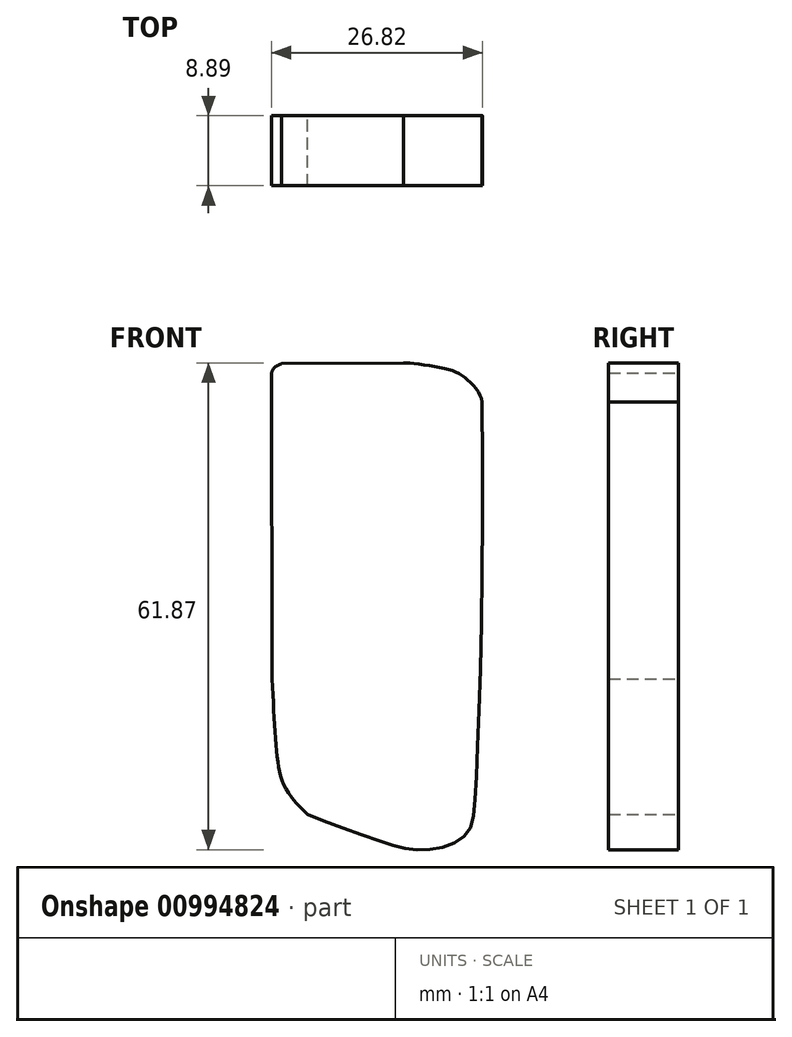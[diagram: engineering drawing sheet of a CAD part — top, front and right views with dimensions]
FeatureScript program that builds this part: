
annotation { "Feature Type Name" : "Feature", "Feature Type Description" : "" }
export const myFeature = defineFeature(function(context is Context, id is Id, definition is map)
    precondition{}
    {
        {
            var Q0;
            Q0=qCreatedBy(makeId("Front.planeOp"),FACE);
            var sketch = newSketch(context, id + "F0", { "sketchPlane" : qUnion([Q0])});
            skPoint(sketch, "E0.middle", {"position": v(0, 0) * mm});
            skPoint(sketch, "E1", {"position": v(0, -29.08) * mm});
            skPoint(sketch, "E2", {"position": v(12.47, -23.64) * mm});
            skPoint(sketch, "E3", {"position": v(4.34, -30.25) * mm});
            skPoint(sketch, "E4", {"position": v(-12.52, -19.64) * mm});
            skPoint(sketch, "E5", {"position": v(-13.33, -8.6) * mm});
            skFitSpline(sketch, "E6", {"points": [v(-8.85, -25.8) * mm, v(-12.52, -19.64) * mm, v(-13.33, -8.6) * mm], "startDerivative": vector(-18.95, 18.38) * mm, "endDerivative": vector(-1.44, 23.76) * mm});
            skPoint(sketch, "E7", {"position": v(13.33, 26.58) * mm});
            skPoint(sketch, "E8", {"position": v(11.46, 29.43) * mm});
            skPoint(sketch, "E9", {"position": v(8.4, 30.87) * mm});
            skPoint(sketch, "E10", {"position": v(3.38, 31.54) * mm});
            skFitSpline(sketch, "E11", {"points": [v(13.33, 26.58) * mm, v(11.46, 29.43) * mm, v(8.4, 30.87) * mm, v(3.38, 31.54) * mm], "startDerivative": vector(-0.35, 9.05) * mm, "endDerivative": vector(-6.19, 0.04) * mm});
            skPoint(sketch, "E12", {"position": v(-13.2, 30.7) * mm});
            skPoint(sketch, "E13", {"position": v(-12.6, 31.23) * mm});
            skPoint(sketch, "E14", {"position": v(-12.1, 31.42) * mm});
            skPoint(sketch, "E15", {"position": v(-13.39, 30.26) * mm});
            skFitSpline(sketch, "E16", {"points": [v(-13.39, 30.26) * mm, v(-13.2, 30.7) * mm, v(-12.6, 31.23) * mm, v(-12.1, 31.42) * mm], "startDerivative": vector(0.02, 0.4) * mm, "endDerivative": vector(0.33, 0.08) * mm});
            skLineSegment(sketch, "E17", {"start": v(-13.33, -8.6) * mm, "end": v(-13.39, 30.26) * mm});
            skLineSegment(sketch, "E18", {"start": v(-12.1, 31.42) * mm, "end": v(3.38, 31.54) * mm});
            skFitSpline(sketch, "E19", {"points": [v(-8.85, -25.8) * mm, v(0, -29.08) * mm, v(4.34, -30.25) * mm, v(8.4, -30) * mm, v(11.45, -28.22) * mm, v(12.47, -23.64) * mm, v(13.33, 26.58) * mm], "startDerivative": vector(41.09, -18.69) * mm, "endDerivative": vector(-2.72, 177.49) * mm});
            skSolve(sketch);
        }
        {
            var Q0;
            Q0=makeQuery(id+"F0.imprint","IMPRINT",FACE,{"disambiguationData":[TD([[makeQuery(id+"F0.imprint","IMPRINT",EDGE,{"derivedFrom":sQuery(id+"F0.wireOp",EDGE,"E6")}),-1.0]])]});
            extrude(context, id + "F1", {"entities" : qUnion([Q0]), "depth" : 8.9 * mm, "offsetDistance" : 25.4 * mm});
        }
    });
